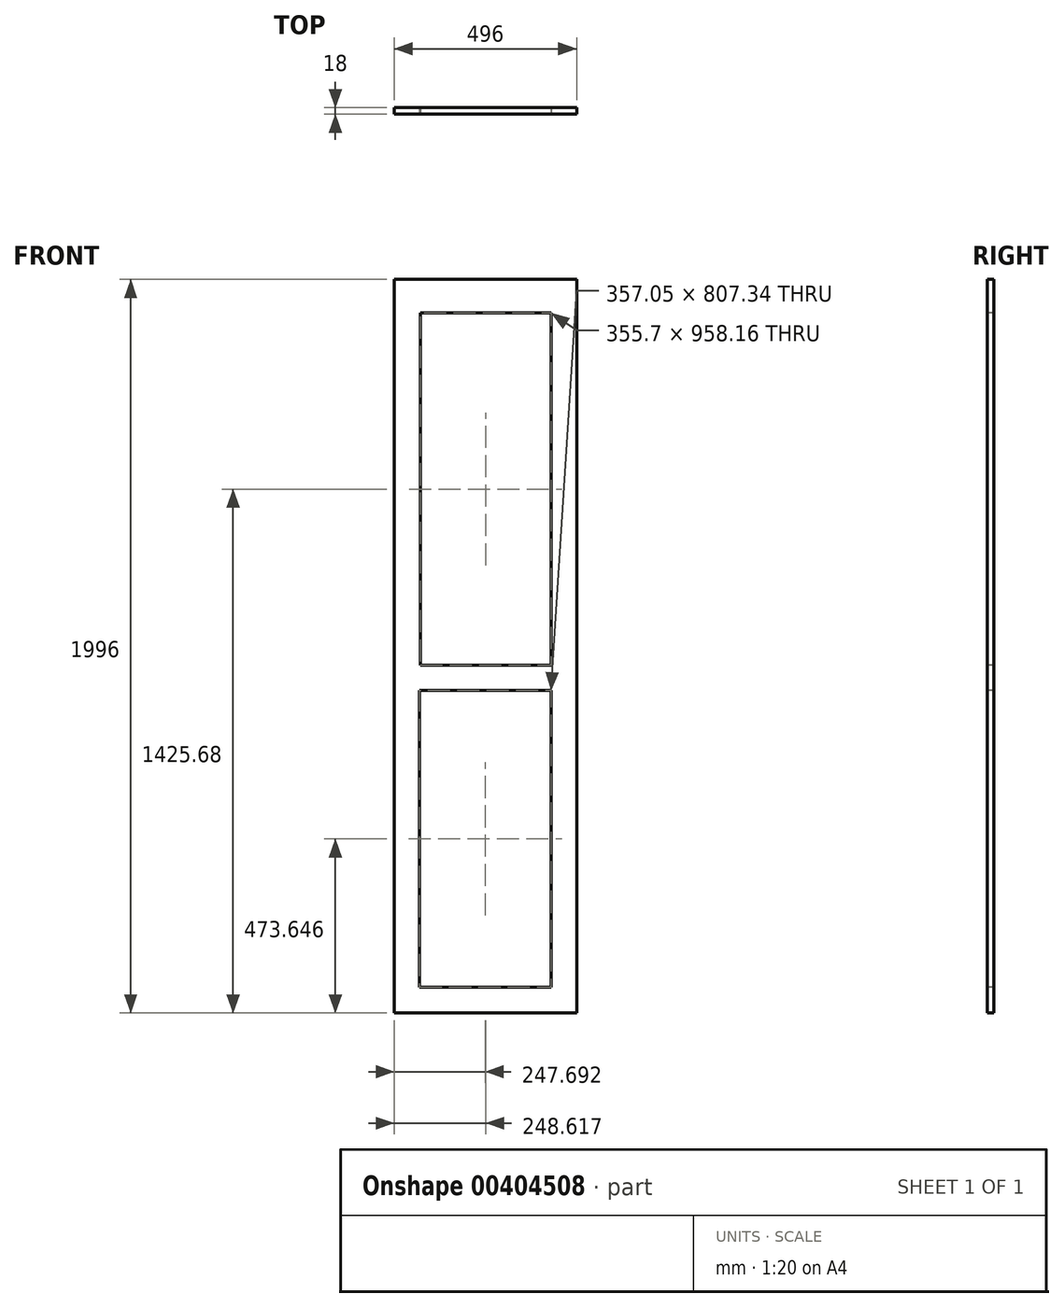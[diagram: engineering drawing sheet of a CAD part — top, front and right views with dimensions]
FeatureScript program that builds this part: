
annotation { "Feature Type Name" : "Feature", "Feature Type Description" : "" }
export const myFeature = defineFeature(function(context is Context, id is Id, definition is map)
    precondition{}
    {
        {
            var Q0;
            Q0=qCreatedBy(makeId("Front.planeOp"),FACE);
            var sketch = newSketch(context, id + "F0", { "sketchPlane" : qUnion([Q0])});
            skLineSegment(sketch, "E0.bottom", {"start": v(0, 0) * mm, "end": v(50.52, 0) * mm});
            skLineSegment(sketch, "E0.top", {"start": v(0, 63.5) * mm, "end": v(50.52, 63.5) * mm});
            skLineSegment(sketch, "E0.left", {"start": v(0, 0) * mm, "end": v(0, 63.5) * mm});
            skLineSegment(sketch, "E0.right", {"start": v(50.52, 0) * mm, "end": v(50.52, 63.5) * mm});
            skSolve(sketch);
        }
        {
            var Q0;
            Q0=makeQuery(id+"F0.imprint","IMPRINT",FACE,{"disambiguationData":[TD([[makeQuery(id+"F0.imprint","IMPRINT",EDGE,{"derivedFrom":sQuery(id+"F0.wireOp",EDGE,"E0.bottom")}),1.0]])]});
            extrude(context, id + "F1", {"entities" : qUnion([Q0]), "depth" : 18 * mm});
        }
        {
            var Q0;
            Q0=makeQuery(id+"F1.opExtrude","SWEPT_FACE",FACE,{"disambiguationData":[OSD([sQuery(id+"F0.wireOp",EDGE,"E0.left")])]});
            extrude(context, id + "F2", {"entities" : qUnion([Q0]), "operationType" : NewBodyOperationType.ADD, "oppositeDirection" : true, "depth" : 496 * mm});
        }
        {
            var Q0;
            {var subQ0=sQuery(id+"F0.wireOp",EDGE,"E0.bottom");Q0=makeQuery(id+"F2.boolean.opBoolean","MERGE",FACE,{"derivedFrom":[makeQuery(id+"F1.opExtrude","SWEPT_FACE",FACE,{"disambiguationData":[OSD([subQ0])]}),makeQuery(id+"F2.opExtrude","SWEPT_FACE",FACE,{"disambiguationData":[OSD([subQ0,sQuery(id+"F0.wireOp",EDGE,"E0.left")])]})]});}
            extrude(context, id + "F3", {"entities" : qUnion([Q0]), "operationType" : NewBodyOperationType.ADD, "oppositeDirection" : true, "depth" : 1996 * mm});
        }
        {
            var Q0;
            {var subQ0=sQuery(id+"F0.wireOp",EDGE,"E0.left");var subQ1=sQuery(id+"F0.wireOp",EDGE,"E0.bottom");Q0=makeQuery(id+"F3.boolean.opBoolean","MERGE",FACE,{"derivedFrom":[makeQuery(id+"F2.boolean.opBoolean","MERGE",FACE,{"derivedFrom":[makeQuery(id+"F1.opExtrude","CAP_FACE",FACE,{"disambiguationData":[OSD([subQ1,sQuery(id+"F0.wireOp",EDGE,"E0.top"),subQ0,sQuery(id+"F0.wireOp",EDGE,"E0.right")])],"isStart":false}),makeQuery(id+"F2.opExtrude","SWEPT_FACE",FACE,{"disambiguationData":[OSD([subQ0]),TDD([makeQuery(id+"F1.opExtrude","CAP_EDGE",EDGE,{"disambiguationData":[OSD([subQ0])],"isStart":false})])]})]}),makeQuery(id+"F3.opExtrude","SWEPT_FACE",FACE,{"disambiguationData":[OSD([subQ1,subQ0]),TDD([makeQuery(id+"F2.boolean.opBoolean","MERGE",EDGE,{"derivedFrom":[makeQuery(id+"F1.opExtrude","CAP_EDGE",EDGE,{"disambiguationData":[OSD([subQ1])],"isStart":false}),makeQuery(id+"F2.opExtrude","SWEPT_EDGE",EDGE,{"disambiguationData":[OSD([subQ1,subQ0]),TDD([makeQuery(id+"F1.opExtrude","CAP_VERTEX",VERTEX,{"disambiguationData":[OSD([subQ1,subQ0])],"isStart":false})])]})]})])]})]});}
            var sketch = newSketch(context, id + "F4", { "sketchPlane" : qUnion([Q0])});
            skLineSegment(sketch, "E1.bottom", {"start": v(65.17, 1024.31) * mm, "end": v(382.22, 1024.31) * mm});
            skLineSegment(sketch, "E1.top", {"start": v(65.17, 351.98) * mm, "end": v(382.22, 351.98) * mm});
            skLineSegment(sketch, "E1.left", {"start": v(65.17, 1024.31) * mm, "end": v(65.17, 351.98) * mm});
            skLineSegment(sketch, "E1.right", {"start": v(382.22, 1024.31) * mm, "end": v(382.22, 351.98) * mm});
            skSolve(sketch);
        }
        {
            var Q0;
            Q0=makeQuery(id+"F4.imprint","IMPRINT",FACE,{"disambiguationData":[TD([[makeQuery(id+"F4.imprint","IMPRINT",EDGE,{"derivedFrom":sQuery(id+"F4.wireOp",EDGE,"E1.bottom")}),-1.0]])]});
            extrude(context, id + "F5", {"entities" : qUnion([Q0]), "operationType" : NewBodyOperationType.REMOVE, "oppositeDirection" : true, "depth" : 18 * mm});
        }
        {
            var Q0;
            Q0=makeQuery(id+"F5.boolean.opBoolean","COPY",FACE,{"derivedFrom":makeQuery(id+"F5.opExtrude","SWEPT_FACE",FACE,{"disambiguationData":[OSD([sQuery(id+"F4.wireOp",EDGE,"E1.left")])]})});
            extrude(context, id + "F6", {"entities" : qUnion([Q0]), "operationType" : NewBodyOperationType.ADD, "depth" : 66 * mm});
        }
        {
            var Q0;
            Q0=makeQuery(id+"F6.opExtrude","CAP_FACE",FACE,{"disambiguationData":[OSD([sQuery(id+"F4.wireOp",EDGE,"E1.left")])],"isStart":false});
            extrude(context, id + "F7", {"entities" : qUnion([Q0]), "operationType" : NewBodyOperationType.REMOVE, "oppositeDirection" : true, "depth" : 68 * mm});
        }
        {
            var Q0;
            Q0=makeQuery(id+"F7.boolean.opBoolean","COPY",FACE,{"derivedFrom":makeQuery(id+"F7.opExtrude","CAP_FACE",FACE,{"disambiguationData":[OSD([sQuery(id+"F4.wireOp",EDGE,"E1.left")])],"isStart":false})});
            extrude(context, id + "F8", {"entities" : qUnion([Q0]), "operationType" : NewBodyOperationType.ADD, "depth" : 6 * mm});
        }
        {
            var Q0;
            {var subQ0=sQuery(id+"F4.wireOp",EDGE,"E1.top");Q0=makeQuery(id+"F7.boolean.opBoolean","MERGE",FACE,{"derivedFrom":[makeQuery(id+"F5.boolean.opBoolean","COPY",FACE,{"derivedFrom":makeQuery(id+"F5.opExtrude","SWEPT_FACE",FACE,{"disambiguationData":[OSD([subQ0])]})}),makeQuery(id+"F7.opExtrude","SWEPT_FACE",FACE,{"disambiguationData":[OSD([subQ0,sQuery(id+"F4.wireOp",EDGE,"E1.left")])]})]});}
            extrude(context, id + "F9", {"entities" : qUnion([Q0]), "operationType" : NewBodyOperationType.REMOVE, "oppositeDirection" : true, "depth" : 282 * mm});
        }
        {
            var Q0;
            {var subQ0=sQuery(id+"F4.wireOp",EDGE,"E1.right");Q0=makeQuery(id+"F9.boolean.opBoolean","MERGE",FACE,{"derivedFrom":[makeQuery(id+"F5.boolean.opBoolean","COPY",FACE,{"derivedFrom":makeQuery(id+"F5.opExtrude","SWEPT_FACE",FACE,{"disambiguationData":[OSD([subQ0])]})}),makeQuery(id+"F9.opExtrude","SWEPT_FACE",FACE,{"disambiguationData":[OSD([sQuery(id+"F4.wireOp",EDGE,"E1.top"),subQ0])]})]});}
            extrude(context, id + "F10", {"entities" : qUnion([Q0]), "operationType" : NewBodyOperationType.REMOVE, "oppositeDirection" : true, "depth" : 44 * mm});
        }
        {
            var Q0;
            {var subQ0=sQuery(id+"F4.wireOp",EDGE,"E1.bottom");Q0=makeQuery(id+"F10.boolean.opBoolean","MERGE",FACE,{"derivedFrom":[makeQuery(id+"F7.boolean.opBoolean","MERGE",FACE,{"derivedFrom":[makeQuery(id+"F5.boolean.opBoolean","COPY",FACE,{"derivedFrom":makeQuery(id+"F5.opExtrude","SWEPT_FACE",FACE,{"disambiguationData":[OSD([subQ0])]})}),makeQuery(id+"F7.opExtrude","SWEPT_FACE",FACE,{"disambiguationData":[OSD([subQ0,sQuery(id+"F4.wireOp",EDGE,"E1.left")])]})]}),makeQuery(id+"F10.opExtrude","SWEPT_FACE",FACE,{"disambiguationData":[OSD([subQ0,sQuery(id+"F4.wireOp",EDGE,"E1.right")])]})]});}
            extrude(context, id + "F11", {"entities" : qUnion([Q0]), "operationType" : NewBodyOperationType.ADD, "depth" : 147 * mm});
        }
        {
            var Q0;
            {var subQ0=sQuery(id+"F4.wireOp",EDGE,"E1.right");var subQ1=sQuery(id+"F4.wireOp",EDGE,"E1.bottom");var subQ2=sQuery(id+"F4.wireOp",EDGE,"E1.left");var subQ3=makeQuery(id+"F5.boolean.opBoolean","COPY",EDGE,{"derivedFrom":makeQuery(id+"F5.opExtrude","CAP_EDGE",EDGE,{"disambiguationData":[OSD([subQ2])],"isStart":true})});var subQ4=sQuery(id+"F0.wireOp",EDGE,"E0.left");var subQ5=sQuery(id+"F0.wireOp",EDGE,"E0.bottom");Q0=makeQuery(id+"F11.boolean.opBoolean","MERGE",FACE,{"derivedFrom":[makeQuery(id+"F8.boolean.opBoolean","MERGE",FACE,{"derivedFrom":[makeQuery(id+"F6.boolean.opBoolean","MERGE",FACE,{"derivedFrom":[makeQuery(id+"F3.boolean.opBoolean","MERGE",FACE,{"derivedFrom":[makeQuery(id+"F2.boolean.opBoolean","MERGE",FACE,{"derivedFrom":[makeQuery(id+"F1.opExtrude","CAP_FACE",FACE,{"disambiguationData":[OSD([subQ5,sQuery(id+"F0.wireOp",EDGE,"E0.top"),subQ4,sQuery(id+"F0.wireOp",EDGE,"E0.right")])],"isStart":false}),makeQuery(id+"F2.opExtrude","SWEPT_FACE",FACE,{"disambiguationData":[OSD([subQ4]),TDD([makeQuery(id+"F1.opExtrude","CAP_EDGE",EDGE,{"disambiguationData":[OSD([subQ4])],"isStart":false})])]})]}),makeQuery(id+"F3.opExtrude","SWEPT_FACE",FACE,{"disambiguationData":[OSD([subQ5,subQ4]),TDD([makeQuery(id+"F2.boolean.opBoolean","MERGE",EDGE,{"derivedFrom":[makeQuery(id+"F1.opExtrude","CAP_EDGE",EDGE,{"disambiguationData":[OSD([subQ5])],"isStart":false}),makeQuery(id+"F2.opExtrude","SWEPT_EDGE",EDGE,{"disambiguationData":[OSD([subQ5,subQ4]),TDD([makeQuery(id+"F1.opExtrude","CAP_VERTEX",VERTEX,{"disambiguationData":[OSD([subQ5,subQ4])],"isStart":false})])]})]})])]})]}),makeQuery(id+"F6.opExtrude","SWEPT_FACE",FACE,{"disambiguationData":[OSD([subQ2]),TDD([subQ3])]})]}),makeQuery(id+"F8.opExtrude","SWEPT_FACE",FACE,{"disambiguationData":[OSD([subQ2]),TDD([makeQuery(id+"F7.boolean.opBoolean","COPY",EDGE,{"derivedFrom":makeQuery(id+"F7.opExtrude","CAP_EDGE",EDGE,{"disambiguationData":[OSD([subQ2]),TDD([makeQuery(id+"F6.opExtrude","CAP_EDGE",EDGE,{"disambiguationData":[OSD([subQ2]),TDD([subQ3])],"isStart":false})])],"isStart":false})})])]})]}),makeQuery(id+"F11.opExtrude","SWEPT_FACE",FACE,{"disambiguationData":[OSD([subQ1,subQ2,subQ0]),TDD([makeQuery(id+"F10.boolean.opBoolean","MERGE",EDGE,{"derivedFrom":[makeQuery(id+"F7.boolean.opBoolean","MERGE",EDGE,{"derivedFrom":[makeQuery(id+"F5.boolean.opBoolean","COPY",EDGE,{"derivedFrom":makeQuery(id+"F5.opExtrude","CAP_EDGE",EDGE,{"disambiguationData":[OSD([subQ1])],"isStart":true})}),makeQuery(id+"F7.opExtrude","SWEPT_EDGE",EDGE,{"disambiguationData":[OSD([subQ1,subQ2]),TDD([makeQuery(id+"F6.opExtrude","CAP_VERTEX",VERTEX,{"disambiguationData":[OSD([subQ1,subQ2]),TDD([makeQuery(id+"F5.boolean.opBoolean","COPY",VERTEX,{"derivedFrom":makeQuery(id+"F5.opExtrude","CAP_VERTEX",VERTEX,{"disambiguationData":[OSD([subQ1,subQ2])],"isStart":true})})])],"isStart":false})])]})]}),makeQuery(id+"F10.opExtrude","SWEPT_EDGE",EDGE,{"disambiguationData":[OSD([subQ1,subQ0]),TDD([makeQuery(id+"F5.boolean.opBoolean","COPY",VERTEX,{"derivedFrom":makeQuery(id+"F5.opExtrude","CAP_VERTEX",VERTEX,{"disambiguationData":[OSD([subQ1,subQ0])],"isStart":true})})])]})]})])]})]});}
            var sketch = newSketch(context, id + "F12", { "sketchPlane" : qUnion([Q0])});
            skLineSegment(sketch, "E2.bottom", {"start": v(70.77, 1021.6) * mm, "end": v(428.47, 1021.6) * mm});
            skLineSegment(sketch, "E2.top", {"start": v(70.77, 1904.76) * mm, "end": v(428.47, 1904.76) * mm});
            skLineSegment(sketch, "E2.left", {"start": v(70.77, 1021.6) * mm, "end": v(70.77, 1904.76) * mm});
            skLineSegment(sketch, "E2.right", {"start": v(428.47, 1021.6) * mm, "end": v(428.47, 1904.76) * mm});
            skSolve(sketch);
        }
        {
            var Q0;
            Q0=makeQuery(id+"F12.imprint","IMPRINT",FACE,{"disambiguationData":[TD([[makeQuery(id+"F12.imprint","IMPRINT",EDGE,{"derivedFrom":sQuery(id+"F12.wireOp",EDGE,"E2.bottom")}),1.0]])]});
            extrude(context, id + "F13", {"entities" : qUnion([Q0]), "operationType" : NewBodyOperationType.REMOVE, "oppositeDirection" : true, "depth" : 18 * mm});
        }
        {
            var Q0;
            Q0=makeQuery(id+"F13.boolean.opBoolean","COPY",FACE,{"derivedFrom":makeQuery(id+"F13.opExtrude","SWEPT_FACE",FACE,{"disambiguationData":[OSD([sQuery(id+"F12.wireOp",EDGE,"E2.bottom")])]})});
            extrude(context, id + "F14", {"entities" : qUnion([Q0]), "operationType" : NewBodyOperationType.REMOVE, "oppositeDirection" : true, "depth" : 75 * mm});
        }
        {
            var Q0;
            {var subQ0=sQuery(id+"F12.wireOp",EDGE,"E2.right");Q0=makeQuery(id+"F14.boolean.opBoolean","MERGE",FACE,{"derivedFrom":[makeQuery(id+"F13.boolean.opBoolean","COPY",FACE,{"derivedFrom":makeQuery(id+"F13.opExtrude","SWEPT_FACE",FACE,{"disambiguationData":[OSD([subQ0])]})}),makeQuery(id+"F14.opExtrude","SWEPT_FACE",FACE,{"disambiguationData":[OSD([sQuery(id+"F12.wireOp",EDGE,"E2.bottom"),subQ0])]})]});}
            extrude(context, id + "F15", {"entities" : qUnion([Q0]), "operationType" : NewBodyOperationType.ADD, "depth" : 2 * mm});
        }
    });
